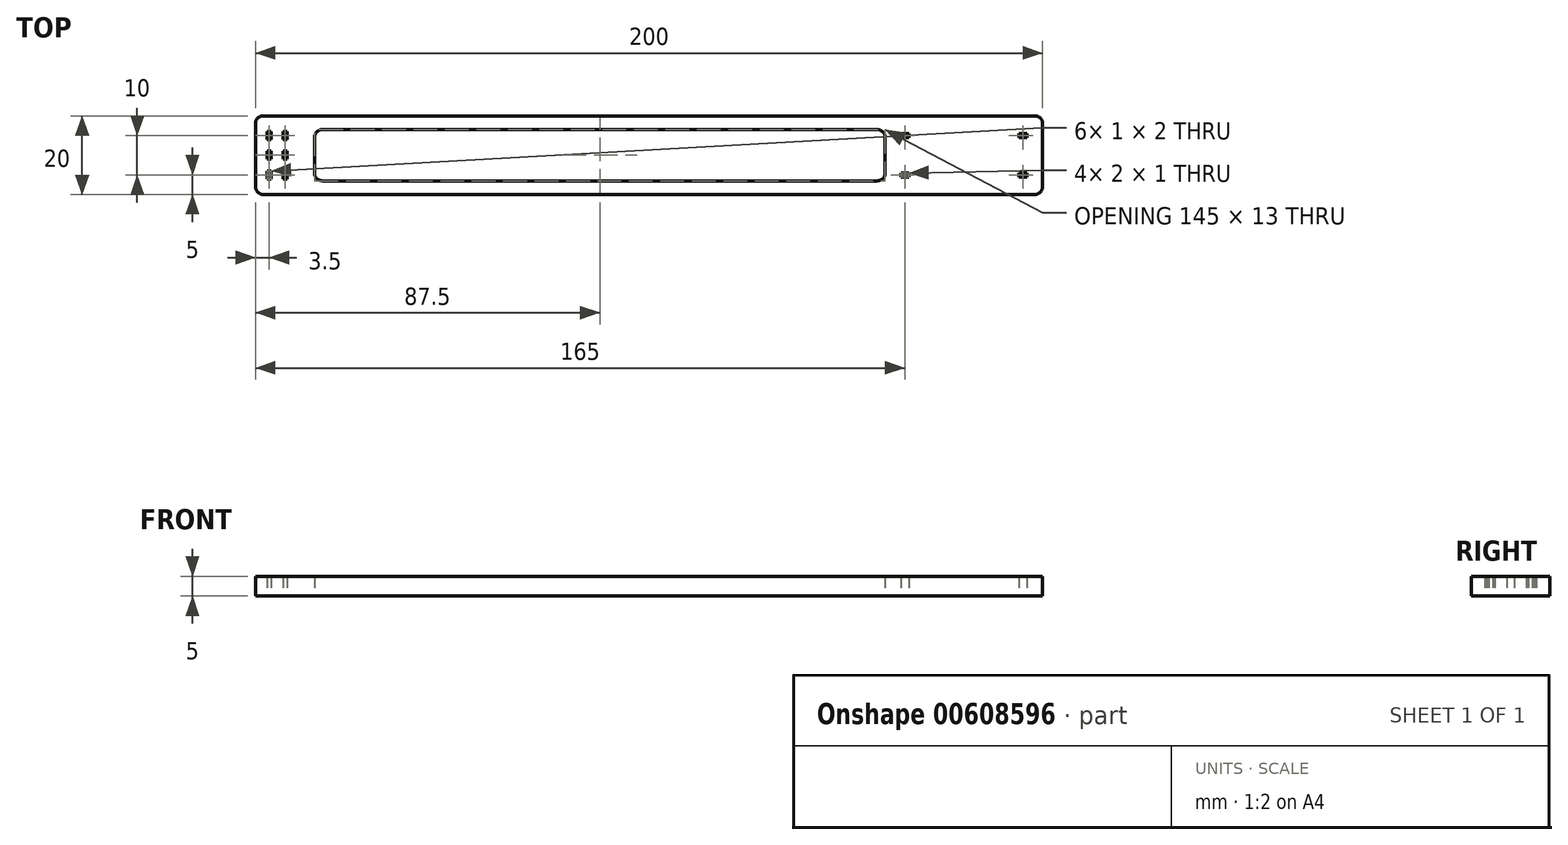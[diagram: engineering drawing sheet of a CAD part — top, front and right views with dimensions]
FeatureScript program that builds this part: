
annotation { "Feature Type Name" : "Feature", "Feature Type Description" : "" }
export const myFeature = defineFeature(function(context is Context, id is Id, definition is map)
    precondition{}
    {
        {
            var Q0;
            Q0=qCreatedBy(makeId("Top.planeOp"),FACE);
            var sketch = newSketch(context, id + "F0", { "sketchPlane" : qUnion([Q0])});
            skLineSegment(sketch, "E0.bottom", {"start": v(2, 0) * mm, "end": v(198, 0) * mm});
            skLineSegment(sketch, "E0.top", {"start": v(2, 20) * mm, "end": v(198, 20) * mm});
            skLineSegment(sketch, "E0.left", {"start": v(0, 2) * mm, "end": v(0, 18) * mm});
            skLineSegment(sketch, "E1.right", {"start": v(200, 18) * mm, "end": v(200, 2) * mm});
            skLineSegment(sketch, "E2", {"start": v(200, 10) * mm, "end": v(0, 10) * mm, "construction": true});
            skLineSegment(sketch, "E3", {"start": v(4, 20) * mm, "end": v(4, 10) * mm, "construction": true});
            skLineSegment(sketch, "E4", {"start": v(5.5, 20) * mm, "end": v(5.5, 10) * mm, "construction": true});
            skLineSegment(sketch, "E5.bottom", {"start": v(3, 16) * mm, "end": v(4, 16) * mm});
            skLineSegment(sketch, "E5.top", {"start": v(3, 14) * mm, "end": v(4, 14) * mm});
            skLineSegment(sketch, "E5.left", {"start": v(3, 16) * mm, "end": v(3, 14) * mm});
            skLineSegment(sketch, "E5.right", {"start": v(4, 16) * mm, "end": v(4, 14) * mm});
            skLineSegment(sketch, "E6.bottom", {"start": v(3, 11) * mm, "end": v(4, 11) * mm});
            skLineSegment(sketch, "E6.top", {"start": v(3, 9) * mm, "end": v(4, 9) * mm});
            skLineSegment(sketch, "E6.left", {"start": v(3, 11) * mm, "end": v(3, 9) * mm});
            skLineSegment(sketch, "E6.right", {"start": v(4, 11) * mm, "end": v(4, 9) * mm});
            skLineSegment(sketch, "E7", {"start": v(3, 15) * mm, "end": v(4, 15) * mm, "construction": true});
            skLineSegment(sketch, "E8", {"start": v(3, 10) * mm, "end": v(4, 10) * mm});
            skLineSegment(sketch, "E9.MirrorCS", {"start": v(8, 14) * mm, "end": v(7, 14) * mm});
            skLineSegment(sketch, "E10.MirrorCS", {"start": v(8, 16) * mm, "end": v(8, 14) * mm});
            skLineSegment(sketch, "E11.MirrorCS", {"start": v(8, 16) * mm, "end": v(7, 16) * mm});
            skLineSegment(sketch, "E12.MirrorCS", {"start": v(8, 11) * mm, "end": v(7, 11) * mm});
            skLineSegment(sketch, "E13.MirrorCS", {"start": v(8, 11) * mm, "end": v(8, 9) * mm});
            skLineSegment(sketch, "E14.MirrorCS", {"start": v(7, 11) * mm, "end": v(7, 9) * mm});
            skLineSegment(sketch, "E15.MirrorCS", {"start": v(8, 9) * mm, "end": v(7, 9) * mm});
            skLineSegment(sketch, "E16.MirrorCS", {"start": v(7, 16) * mm, "end": v(7, 14) * mm});
            skLineSegment(sketch, "E17.MirrorCS", {"start": v(3, 5) * mm, "end": v(4, 5) * mm, "construction": true});
            skLineSegment(sketch, "E18.MirrorCS", {"start": v(3, 6) * mm, "end": v(4, 6) * mm});
            skLineSegment(sketch, "E19.MirrorCS", {"start": v(8, 4) * mm, "end": v(7, 4) * mm});
            skLineSegment(sketch, "E20.MirrorCS", {"start": v(8, 6) * mm, "end": v(7, 6) * mm});
            skLineSegment(sketch, "E21.MirrorCS", {"start": v(3, 4) * mm, "end": v(4, 4) * mm});
            skLineSegment(sketch, "E22.MirrorCS", {"start": v(3, 4) * mm, "end": v(3, 6) * mm});
            skLineSegment(sketch, "E23.MirrorCS", {"start": v(4, 4) * mm, "end": v(4, 6) * mm});
            skLineSegment(sketch, "E24.MirrorCS", {"start": v(7, 4) * mm, "end": v(7, 6) * mm});
            skLineSegment(sketch, "E25.MirrorCS", {"start": v(8, 4) * mm, "end": v(8, 6) * mm});
            skLineSegment(sketch, "E26.bottom", {"start": v(158, 16.5) * mm, "end": v(17, 16.5) * mm});
            skLineSegment(sketch, "E26.top", {"start": v(158, 3.5) * mm, "end": v(17, 3.5) * mm});
            skLineSegment(sketch, "E26.left", {"start": v(160, 14.5) * mm, "end": v(160, 5.5) * mm});
            skLineSegment(sketch, "E26.right", {"start": v(15, 14.5) * mm, "end": v(15, 5.5) * mm});
            skPoint(sketch, "E26.middle", {"position": v(87.5, 10) * mm});
            skPoint(sketch, "E27.visualSharp", {"position": v(200, 20) * mm});
            skArc(sketch, "E27.filletArc", {"start": v(200, 18) * mm, "mid": v(199.41, 19.41) * mm, "end": v(198, 20) * mm});
            skPoint(sketch, "E28.visualSharp", {"position": v(200, 0) * mm});
            skArc(sketch, "E28.filletArc", {"start": v(198, 0) * mm, "mid": v(199.41, 0.59) * mm, "end": v(200, 2) * mm});
            skPoint(sketch, "E29.visualSharp", {"position": v(160, 16.5) * mm});
            skArc(sketch, "E29.filletArc", {"start": v(160, 14.5) * mm, "mid": v(159.41, 15.91) * mm, "end": v(158, 16.5) * mm});
            skPoint(sketch, "E30.visualSharp", {"position": v(160, 3.5) * mm});
            skArc(sketch, "E30.filletArc", {"start": v(158, 3.5) * mm, "mid": v(159.41, 4.09) * mm, "end": v(160, 5.5) * mm});
            skPoint(sketch, "E31.visualSharp", {"position": v(15, 16.5) * mm});
            skArc(sketch, "E31.filletArc", {"start": v(17, 16.5) * mm, "mid": v(15.59, 15.91) * mm, "end": v(15, 14.5) * mm});
            skPoint(sketch, "E32.visualSharp", {"position": v(15, 3.5) * mm});
            skArc(sketch, "E32.filletArc", {"start": v(15, 5.5) * mm, "mid": v(15.59, 4.09) * mm, "end": v(17, 3.5) * mm});
            skPoint(sketch, "E33.visualSharp", {"position": v(0, 20) * mm});
            skArc(sketch, "E33.filletArc", {"start": v(2, 20) * mm, "mid": v(0.59, 19.41) * mm, "end": v(0, 18) * mm});
            skPoint(sketch, "E34.visualSharp", {"position": v(0, 0) * mm});
            skArc(sketch, "E34.filletArc", {"start": v(0, 2) * mm, "mid": v(0.59, 0.59) * mm, "end": v(2, 0) * mm});
            skPoint(sketch, "E35.orphan", {"position": v(175, 10) * mm});
            skCircle(sketch, "E36", {"center": v(180, 10) * mm, "radius": 10 * mm, "construction": true});
            skLineSegment(sketch, "E37", {"start": v(195, 20) * mm, "end": v(195, 10) * mm, "construction": true});
            skLineSegment(sketch, "E38", {"start": v(180, 20) * mm, "end": v(180, 0) * mm, "construction": true});
            skLineSegment(sketch, "E39.bottom", {"start": v(196, 15.5) * mm, "end": v(194, 15.5) * mm});
            skLineSegment(sketch, "E39.top", {"start": v(196, 14.5) * mm, "end": v(194, 14.5) * mm});
            skLineSegment(sketch, "E39.left", {"start": v(196, 15.5) * mm, "end": v(196, 14.5) * mm});
            skLineSegment(sketch, "E39.right", {"start": v(194, 15.5) * mm, "end": v(194, 14.5) * mm});
            skPoint(sketch, "E39.middle", {"position": v(195, 15) * mm});
            skPoint(sketch, "E40.MirrorP", {"position": v(195, 5) * mm});
            skLineSegment(sketch, "E41.MirrorCS", {"start": v(196, 5.5) * mm, "end": v(194, 5.5) * mm});
            skLineSegment(sketch, "E42.MirrorCS", {"start": v(196, 4.5) * mm, "end": v(196, 5.5) * mm});
            skLineSegment(sketch, "E43.MirrorCS", {"start": v(196, 4.5) * mm, "end": v(194, 4.5) * mm});
            skLineSegment(sketch, "E44.MirrorCS", {"start": v(194, 4.5) * mm, "end": v(194, 5.5) * mm});
            skLineSegment(sketch, "E45.MirrorCS", {"start": v(166, 15.5) * mm, "end": v(166, 14.5) * mm});
            skPoint(sketch, "E46.MirrorP", {"position": v(165, 15) * mm});
            skLineSegment(sketch, "E47.MirrorCS", {"start": v(164, 15.5) * mm, "end": v(166, 15.5) * mm});
            skLineSegment(sketch, "E48.MirrorCS", {"start": v(164, 15.5) * mm, "end": v(164, 14.5) * mm});
            skLineSegment(sketch, "E49.MirrorCS", {"start": v(164, 14.5) * mm, "end": v(166, 14.5) * mm});
            skPoint(sketch, "E50.MirrorP", {"position": v(165, 5) * mm});
            skLineSegment(sketch, "E51.MirrorCS", {"start": v(164, 5.5) * mm, "end": v(166, 5.5) * mm});
            skLineSegment(sketch, "E52.MirrorCS", {"start": v(166, 4.5) * mm, "end": v(166, 5.5) * mm});
            skLineSegment(sketch, "E53.MirrorCS", {"start": v(164, 4.5) * mm, "end": v(166, 4.5) * mm});
            skLineSegment(sketch, "E54.MirrorCS", {"start": v(164, 4.5) * mm, "end": v(164, 5.5) * mm});
            skSolve(sketch);
        }
        {
            var Q0;
            Q0=qSketchRegion(id+"F0",true);
            extrude(context, id + "F1", {"entities" : qUnion([Q0]), "depth" : 5 * mm, "offsetDistance" : 25 * mm});
        }
    });
